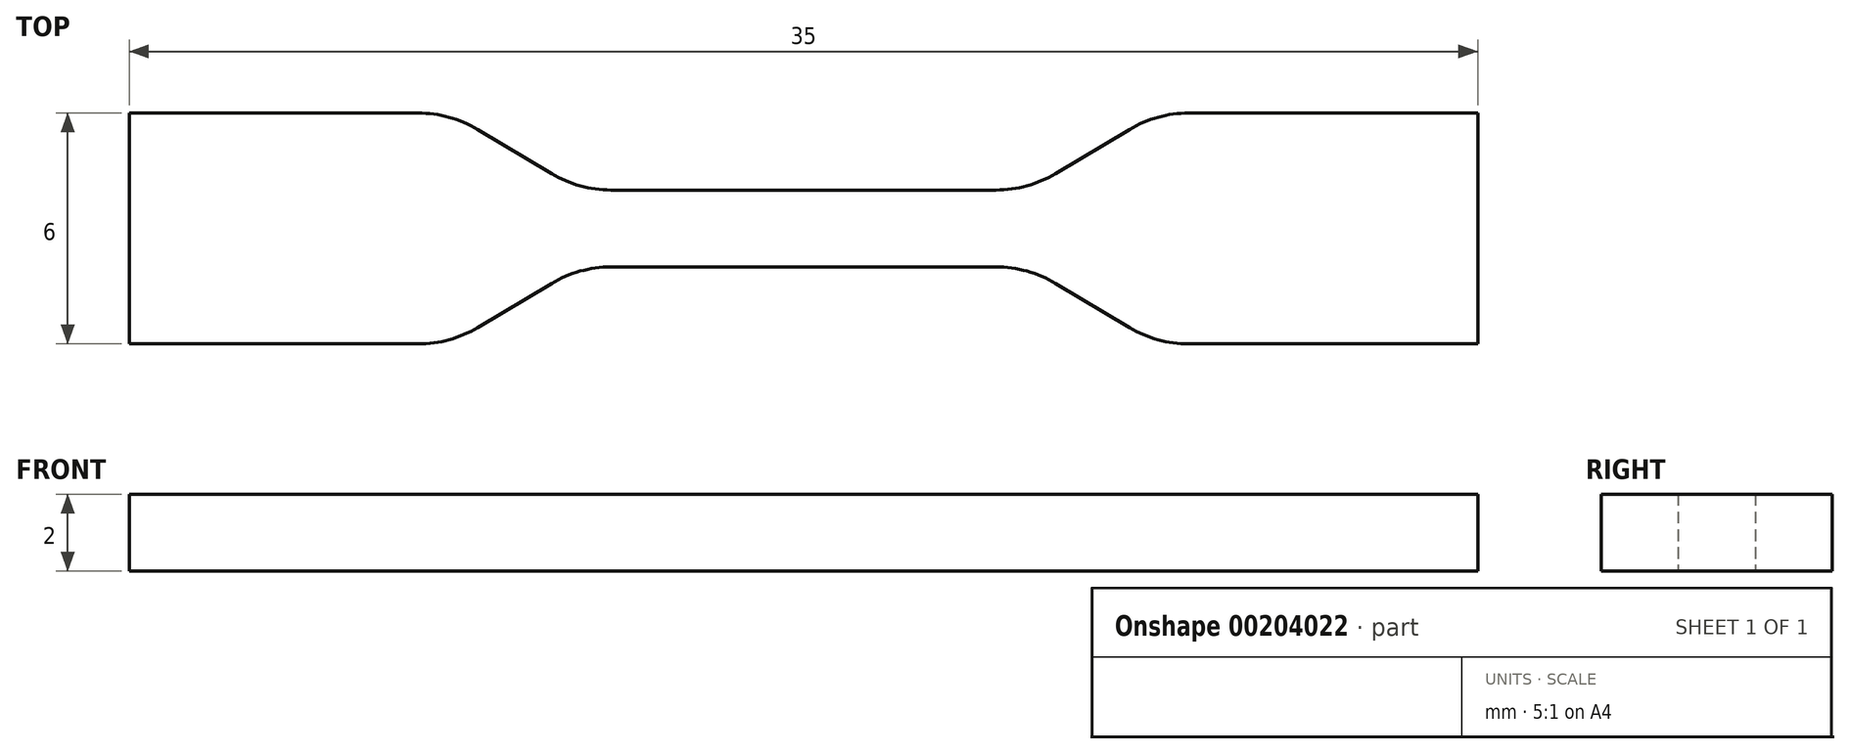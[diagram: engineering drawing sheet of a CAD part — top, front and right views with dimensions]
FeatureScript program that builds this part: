
annotation { "Feature Type Name" : "Feature", "Feature Type Description" : "" }
export const myFeature = defineFeature(function(context is Context, id is Id, definition is map)
    precondition{}
    {
        {
            var Q0;
            Q0=qCreatedBy(makeId("Top.planeOp"),FACE);
            var sketch = newSketch(context, id + "F0", { "sketchPlane" : qUnion([Q0])});
            skLineSegment(sketch, "E0", {"start": v(0, 0) * mm, "end": v(17.5, 0) * mm, "construction": true});
            skLineSegment(sketch, "E1", {"start": v(0, 0) * mm, "end": v(0, 1) * mm});
            skLineSegment(sketch, "E2", {"start": v(0, 1) * mm, "end": v(5, 1) * mm});
            skLineSegment(sketch, "E3", {"start": v(17.5, 3) * mm, "end": v(17.5, 0) * mm});
            skLineSegment(sketch, "E4", {"start": v(6.54, 1.43) * mm, "end": v(8.46, 2.57) * mm});
            skLineSegment(sketch, "E5", {"start": v(10, 3) * mm, "end": v(17.5, 3) * mm});
            skLineSegment(sketch, "E6", {"start": v(0, 0) * mm, "end": v(17.5, 0) * mm});
            skPoint(sketch, "E7.visualSharp", {"position": v(5.83, 1) * mm});
            skArc(sketch, "E7.filletArc", {"start": v(5, 1) * mm, "mid": v(5.8, 1.1) * mm, "end": v(6.54, 1.43) * mm});
            skPoint(sketch, "E8.visualSharp", {"position": v(9.17, 3) * mm});
            skArc(sketch, "E8.filletArc", {"start": v(10, 3) * mm, "mid": v(9.2, 2.9) * mm, "end": v(8.46, 2.57) * mm});
            skSolve(sketch);
        }
        {
            var Q0;
            Q0=makeQuery(id+"F0.imprint","IMPRINT",FACE,{"disambiguationData":[TD([[makeQuery(id+"F0.imprint","IMPRINT",EDGE,{"derivedFrom":sQuery(id+"F0.wireOp",EDGE,"E1")}),-1.0]])]});
            extrude(context, id + "F1", {"entities" : qUnion([Q0]), "depth" : 2 * mm});
        }
        {
            var Q0;
            Q0=makeQuery(id+"F1.opExtrude","SWEPT_BODY",BODY,{"disambiguationData":[OSD([sQuery(id+"F0.wireOp",EDGE,"E1"),sQuery(id+"F0.wireOp",EDGE,"E2"),sQuery(id+"F0.wireOp",EDGE,"E3"),sQuery(id+"F0.wireOp",EDGE,"E4"),sQuery(id+"F0.wireOp",EDGE,"E5"),sQuery(id+"F0.wireOp",EDGE,"E6")])]});
            var Q1;
            Q1=makeQuery(id+"F1.opExtrude","SWEPT_FACE",FACE,{"disambiguationData":[OSD([sQuery(id+"F0.wireOp",EDGE,"E6")])]});
            mirror(context, id + "F2", {"operationType" : NewBodyOperationType.ADD, "entities" : qUnion([Q0]), "mirrorPlane" : qUnion([Q1])});
        }
        {
            var Q0;
            Q0=makeQuery(id+"F1.opExtrude","SWEPT_BODY",BODY,{"disambiguationData":[OSD([sQuery(id+"F0.wireOp",EDGE,"E1"),sQuery(id+"F0.wireOp",EDGE,"E2"),sQuery(id+"F0.wireOp",EDGE,"E3"),sQuery(id+"F0.wireOp",EDGE,"E4"),sQuery(id+"F0.wireOp",EDGE,"E5"),sQuery(id+"F0.wireOp",EDGE,"E6")])]});
            var Q1;
            {var subQ0=makeQuery(id+"F1.opExtrude","SWEPT_FACE",FACE,{"disambiguationData":[OSD([sQuery(id+"F0.wireOp",EDGE,"E1")])]});Q1=makeQuery(id+"F2.boolean.opBoolean","MERGE",FACE,{"derivedFrom":[subQ0,makeQuery(id+"F2.opPattern","COPY",FACE,{"derivedFrom":subQ0,"instanceName":"1"})]});}
            mirror(context, id + "F3", {"operationType" : NewBodyOperationType.ADD, "entities" : qUnion([Q0]), "mirrorPlane" : qUnion([Q1])});
        }
    });
